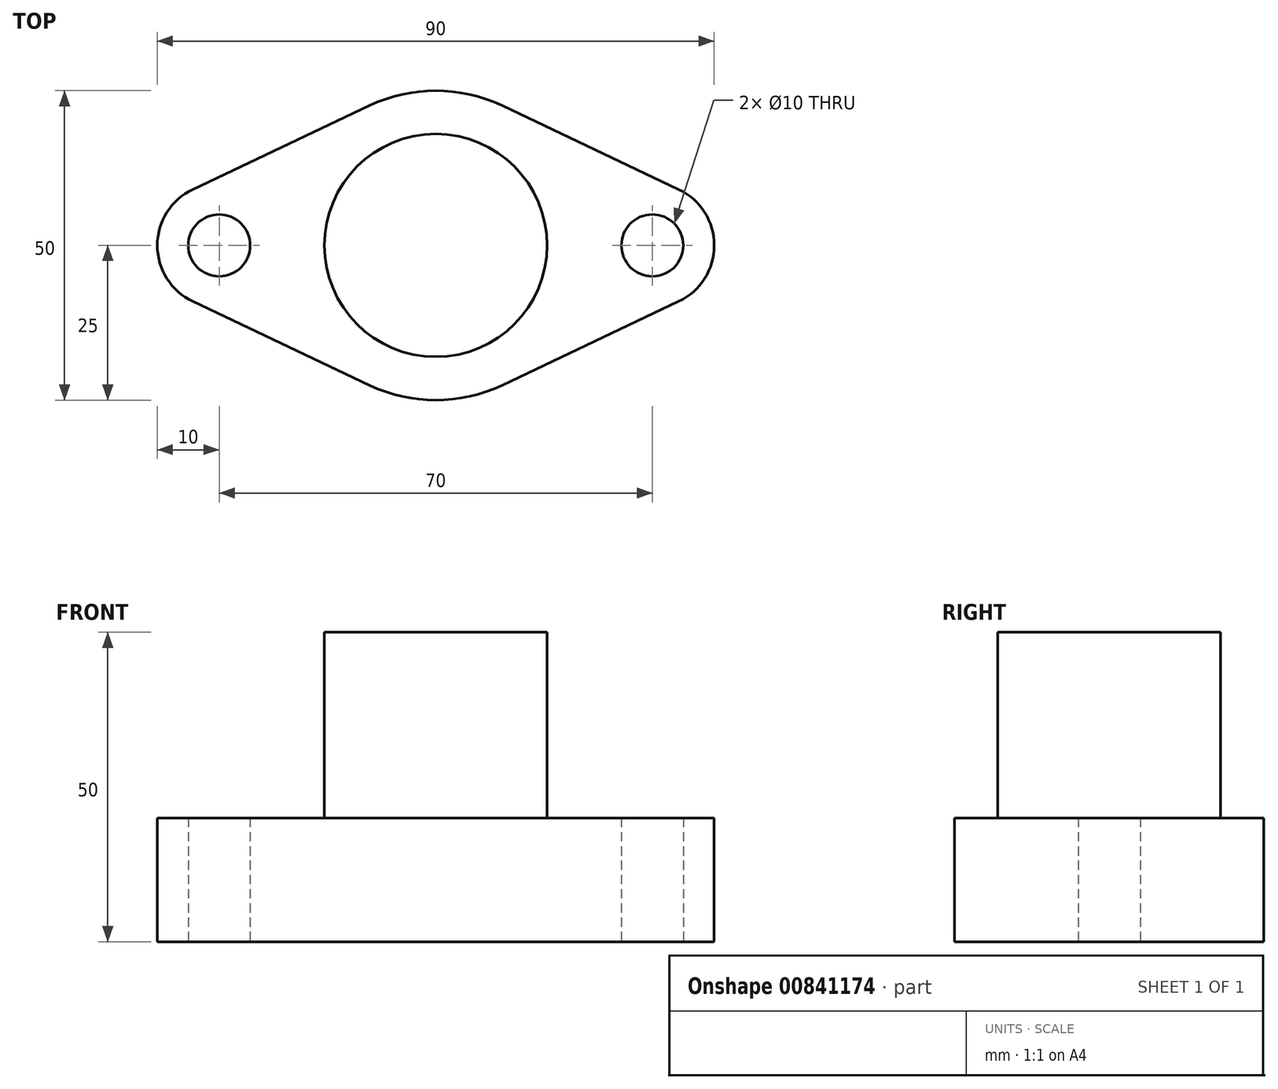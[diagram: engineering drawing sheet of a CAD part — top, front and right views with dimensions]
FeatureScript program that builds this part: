
annotation { "Feature Type Name" : "Feature", "Feature Type Description" : "" }
export const myFeature = defineFeature(function(context is Context, id is Id, definition is map)
    precondition{}
    {
        {
            var Q0;
            Q0=qCreatedBy(makeId("Top.planeOp"),FACE);
            var sketch = newSketch(context, id + "F0", { "sketchPlane" : qUnion([Q0])});
            skCircle(sketch, "E0", {"center": v(0, 0) * mm, "radius": 18 * mm});
            skPoint(sketch, "E1", {"position": v(-35, 0) * mm});
            skPoint(sketch, "E2", {"position": v(35, 0) * mm});
            skCircle(sketch, "E3", {"center": v(-35, 0) * mm, "radius": 5 * mm});
            skCircle(sketch, "E4", {"center": v(35, 0) * mm, "radius": 5 * mm});
            skArc(sketch, "E5", {"start": v(-39.29, 9.04) * mm, "mid": v(-45, 0) * mm, "end": v(-39.29, -9.04) * mm});
            skArc(sketch, "E6", {"start": v(39.29, -9.04) * mm, "mid": v(45, 0) * mm, "end": v(39.29, 9.04) * mm});
            skArc(sketch, "E7", {"start": v(-10.71, -22.59) * mm, "mid": v(0, -25) * mm, "end": v(10.71, -22.59) * mm});
            skLineSegment(sketch, "E8", {"start": v(-39.29, 9.04) * mm, "end": v(-10.71, 22.59) * mm});
            skLineSegment(sketch, "E9", {"start": v(10.71, 22.59) * mm, "end": v(39.29, 9.04) * mm});
            skLineSegment(sketch, "E10", {"start": v(39.29, -9.04) * mm, "end": v(10.71, -22.59) * mm});
            skLineSegment(sketch, "E11", {"start": v(-10.71, -22.59) * mm, "end": v(-39.29, -9.04) * mm});
            skArc(sketch, "E12.trimOffspring", {"start": v(10.71, 22.59) * mm, "mid": v(0, 25) * mm, "end": v(-10.71, 22.59) * mm});
            skSolve(sketch);
        }
        {
            var Q0;
            Q0=makeQuery(id+"F0.imprint","IMPRINT",FACE,{"disambiguationData":[TD([[makeQuery(id+"F0.imprint","IMPRINT",EDGE,{"derivedFrom":sQuery(id+"F0.wireOp",EDGE,"E0")}),-1.0]])]});
            extrude(context, id + "F1", {"entities" : qUnion([Q0]), "depth" : 20 * mm, "offsetDistance" : 25 * mm});
        }
        {
            var Q0;
            Q0=makeQuery(id+"F0.imprint","IMPRINT",FACE,{"disambiguationData":[TD([[makeQuery(id+"F0.imprint","IMPRINT",EDGE,{"derivedFrom":sQuery(id+"F0.wireOp",EDGE,"E0")}),1.0]])]});
            extrude(context, id + "F2", {"entities" : qUnion([Q0]), "operationType" : NewBodyOperationType.ADD, "depth" : 50 * mm, "offsetDistance" : 25 * mm});
        }
    });
